# Revit family: ADB Electric fryers cupboard 600
name_source: partatom
category: Equipement spécialisé
units: mm (PartAtom-declared; Revit-internal decimal feet)

## family parameters
Basée sur le plan de construction = Non
Conserver l'orientation des annotations = Non
Cote de connecteur circulaire = Utiliser le diamètre
Couper avec des vides une fois chargée = Non
Numéro OmniClass = 23.40.40.14.17.11
Partagée = Non
Repère de localisation dans la pièce = Non
Titre OmniClass = Cookers, Ovens, Stoves
Toujours verticalement = Oui
Type d'élément = Normal

## types (3) — shared parameters
Commentaires du type = Ambassade range - Cupboards - Electric fryers
Fabricant = Société Industrielle de Lacanche
URL = https://www.ambassade-de-bourgogne.com
URL Cutsheet = https://www.ambassade-de-bourgogne.com
zero-valued in all types: Elévation par défaut

## per-type parameters (varying)
| type | C | D | Description | Electric power | Height | Operational Current |
| CME 626 FR | 260 mm  [stored 0.853018 ft] | 765 mm  [stored 2.50984 ft] | Cupboard Electric fryers 2x6l -2x6kW | 12000 W | 1012 mm  [stored 3.32021 ft] | 17 A |
| CME 625 FR | 260 mm  [stored 0.853018 ft] | 765 mm  [stored 2.50984 ft] | Cupboard Electric fryers 12x6l - 2x4,5kW | 9000 W | 1012 mm  [stored 3.32021 ft] | 13 A |
| CME 628 FRI | 240 mm  [stored 0.787402 ft] | 715 mm  [stored 2.3458 ft] | Cupboard Electric fryers 2x8l - 2x8kW | 16000 W | 1017 mm  [stored 3.33661 ft] | 23 A |

note: column(s) folded — value = type name in every type: Modèle

note: [stored X ft] marks values corroborated as IEEE doubles in the binary element streams (Revit-internal decimal feet)
